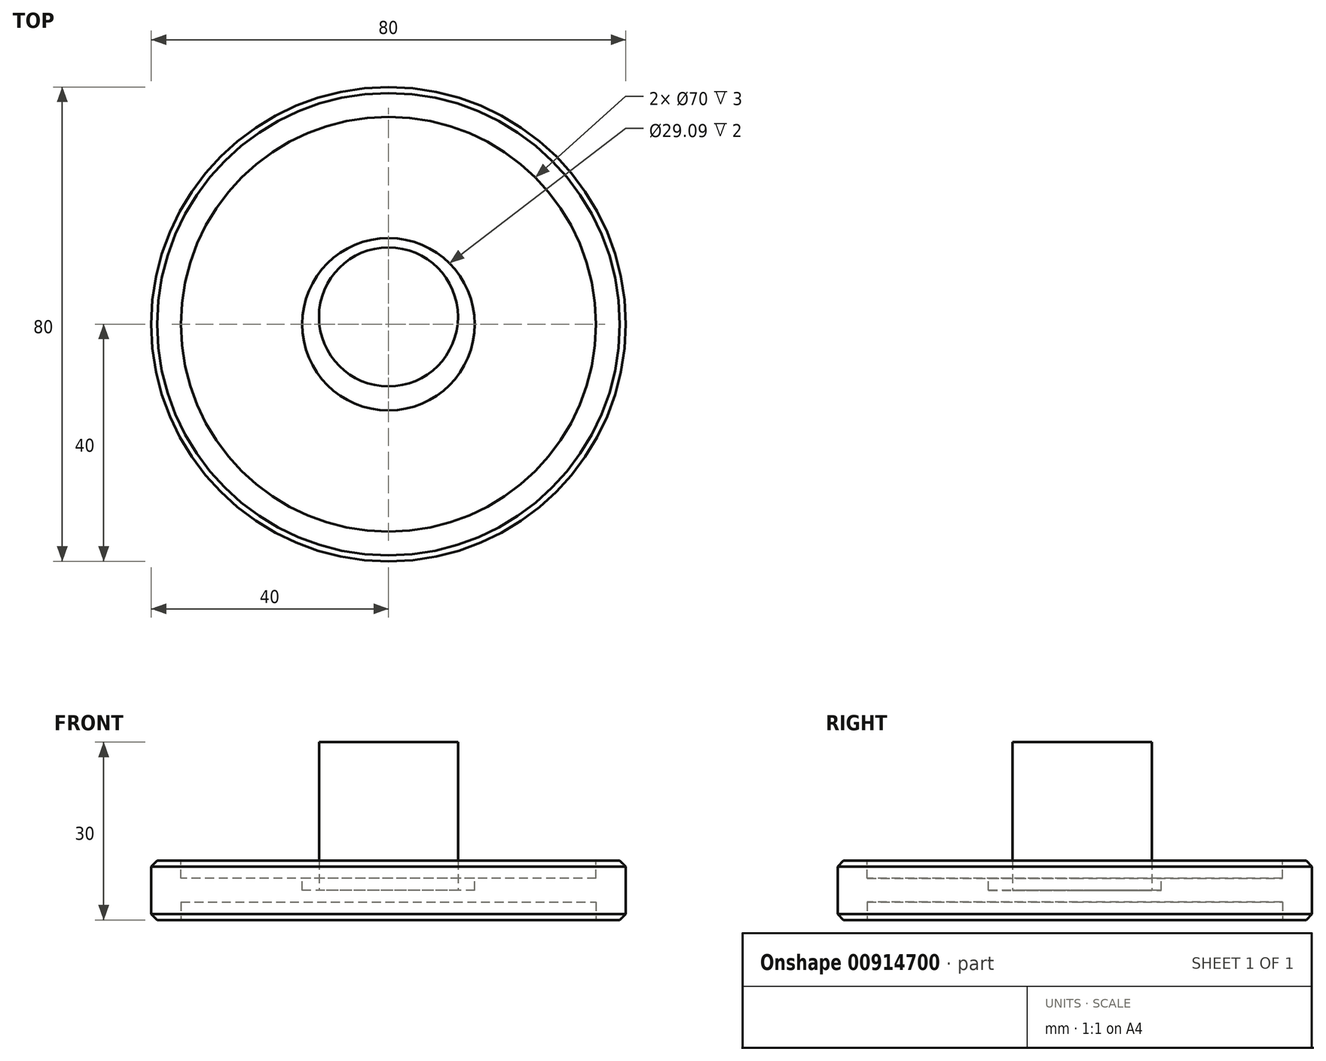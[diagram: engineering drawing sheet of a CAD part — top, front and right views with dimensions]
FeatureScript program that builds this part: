
annotation { "Feature Type Name" : "Feature", "Feature Type Description" : "" }
export const myFeature = defineFeature(function(context is Context, id is Id, definition is map)
    precondition{}
    {
        {
            var Q0;
            Q0=qCreatedBy(makeId("Top.planeOp"),FACE);
            var sketch = newSketch(context, id + "F0", { "sketchPlane" : qUnion([Q0])});
            skCircle(sketch, "E0", {"center": v(0, 0) * mm, "radius": 40 * mm});
            skSolve(sketch);
        }
        {
            var Q0;
            Q0=makeQuery(id+"F0.imprint","IMPRINT",FACE,{"disambiguationData":[TD([[makeQuery(id+"F0.imprint","IMPRINT",EDGE,{"derivedFrom":sQuery(id+"F0.wireOp",EDGE,"E0")}),1.0]])]});
            extrude(context, id + "F1", {"entities" : qUnion([Q0]), "depth" : 10 * mm, "offsetDistance" : 25 * mm});
        }
        {
            var Q0;
            Q0=makeQuery(id+"F1.opExtrude","CAP_FACE",FACE,{"disambiguationData":[OSD([sQuery(id+"F0.wireOp",EDGE,"E0")])],"isStart":false});
            var sketch = newSketch(context, id + "F2", { "sketchPlane" : qUnion([Q0])});
            skCircle(sketch, "E1.0", {"center": v(0, 0) * mm, "radius": 35 * mm});
            skSolve(sketch);
        }
        {
            var Q0;
            Q0=makeQuery(id+"F2.imprint","IMPRINT",FACE,{"disambiguationData":[TD([[makeQuery(id+"F2.imprint","IMPRINT",EDGE,{"derivedFrom":sQuery(id+"F2.wireOp",EDGE,"E1.0")}),1.0]])]});
            extrude(context, id + "F3", {"entities" : qUnion([Q0]), "operationType" : NewBodyOperationType.REMOVE, "oppositeDirection" : true, "depth" : 3 * mm, "offsetDistance" : 25 * mm});
        }
        {
            var Q0;
            Q0=makeQuery(id+"F1.opExtrude","CAP_FACE",FACE,{"disambiguationData":[OSD([sQuery(id+"F0.wireOp",EDGE,"E0")])],"isStart":true});
            var sketch = newSketch(context, id + "F4", { "sketchPlane" : qUnion([Q0])});
            skCircle(sketch, "E2.0", {"center": v(0, 0) * mm, "radius": 35 * mm});
            skSolve(sketch);
        }
        {
            var Q0;
            Q0=makeQuery(id+"F4.imprint","IMPRINT",FACE,{"disambiguationData":[TD([[makeQuery(id+"F4.imprint","IMPRINT",EDGE,{"derivedFrom":sQuery(id+"F4.wireOp",EDGE,"E2.0")}),1.0]])]});
            extrude(context, id + "F5", {"entities" : qUnion([Q0]), "operationType" : NewBodyOperationType.REMOVE, "oppositeDirection" : true, "depth" : 3 * mm, "offsetDistance" : 25 * mm});
        }
        {
            var Q0;
            Q0=makeQuery(id+"F3.boolean.opBoolean","COPY",EDGE,{"derivedFrom":makeQuery(id+"F3.opExtrude","CAP_EDGE",EDGE,{"disambiguationData":[OSD([sQuery(id+"F2.wireOp",EDGE,"E1.0")])],"isStart":true})});
            var Q1;
            Q1=makeQuery(id+"F1.opExtrude","CAP_EDGE",EDGE,{"disambiguationData":[OSD([sQuery(id+"F0.wireOp",EDGE,"E0")])],"isStart":false});
            var Q2;
            Q2=makeQuery(id+"F1.opExtrude","CAP_EDGE",EDGE,{"disambiguationData":[OSD([sQuery(id+"F0.wireOp",EDGE,"E0")])],"isStart":true});
            var Q3;
            Q3=makeQuery(id+"F5.boolean.opBoolean","COPY",EDGE,{"derivedFrom":makeQuery(id+"F5.opExtrude","CAP_EDGE",EDGE,{"disambiguationData":[OSD([sQuery(id+"F4.wireOp",EDGE,"E2.0")])],"isStart":true})});
            chamfer(context, id + "F6", {"entities" : qUnion([Q0, Q1, Q2, Q3]), "width" : 1 * mm, "tangentPropagation" : true});
        }
        {
            var Q0;
            Q0=makeQuery(id+"F3.boolean.opBoolean","COPY",FACE,{"derivedFrom":makeQuery(id+"F3.opExtrude","CAP_FACE",FACE,{"disambiguationData":[OSD([sQuery(id+"F2.wireOp",EDGE,"E1.0")])],"isStart":false})});
            var sketch = newSketch(context, id + "F7", { "sketchPlane" : qUnion([Q0])});
            skCircle(sketch, "E3", {"center": v(0, 0) * mm, "radius": 14.54 * mm});
            skSolve(sketch);
        }
        {
            var Q0;
            Q0=makeQuery(id+"F7.imprint","IMPRINT",FACE,{"disambiguationData":[TD([[makeQuery(id+"F7.imprint","IMPRINT",EDGE,{"derivedFrom":sQuery(id+"F7.wireOp",EDGE,"E3")}),1.0]])]});
            extrude(context, id + "F8", {"entities" : qUnion([Q0]), "operationType" : NewBodyOperationType.REMOVE, "oppositeDirection" : true, "depth" : 2 * mm, "offsetDistance" : 25 * mm});
        }
        {
            var Q0;
            Q0=makeQuery(id+"F8.boolean.opBoolean","COPY",FACE,{"derivedFrom":makeQuery(id+"F8.opExtrude","CAP_FACE",FACE,{"disambiguationData":[OSD([sQuery(id+"F7.wireOp",EDGE,"E3")])],"isStart":false})});
            var sketch = newSketch(context, id + "F9", { "sketchPlane" : qUnion([Q0])});
            skCircle(sketch, "E4", {"center": v(0, 1.24) * mm, "radius": 11.72 * mm});
            skSolve(sketch);
        }
        {
            var Q0;
            Q0=makeQuery(id+"F9.imprint","IMPRINT",FACE,{"disambiguationData":[TD([[makeQuery(id+"F9.imprint","IMPRINT",EDGE,{"derivedFrom":sQuery(id+"F9.wireOp",EDGE,"E4")}),1.0]])]});
            extrude(context, id + "F10", {"entities" : qUnion([Q0]), "operationType" : NewBodyOperationType.ADD, "depth" : 25 * mm, "offsetDistance" : 25 * mm});
        }
    });
